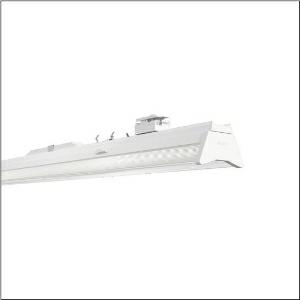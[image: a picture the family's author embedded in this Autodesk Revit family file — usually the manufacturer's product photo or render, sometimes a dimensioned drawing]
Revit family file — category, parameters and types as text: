
# Revit family: licross_r__21_performance_ho_52td16cn4c5m_c92a
name_source: partatom
category: Lighting Fixtures
units: mm (PartAtom-declared; Revit-internal decimal feet)

## family parameters
Cut with Voids When Loaded = No
Host = Face
Light Source = No
Part Type = Normal
Room Calculation Point = No
Round Connector Dimension = Use Diameter
Shared = No

## types (1)
- --- (1 x LED, 12610 lm, 68.9 W, 4000K)
    Apparent Load = 69 VA
    CIE Flux Codes = 63 87 95 78 100
    Color Rendering = 80
    Color Temperature = 4000K
    Default Elevation = 1800 mm
    Description = Licross® 21 Performance HO, luminaire insert, of sheet steel, galvanised, coil coated, white, length: 1.500mm, width: 120mm, height: 123mm, LED rated luminous flux: 12.610lm, light colour: 840, control gear: ON/OFF Multilumen, CLOi, control gear: ECG Multilumen, with plug, 3-pole, with phase selection, mains connection: 220..240V, AC, 50/60Hz, start of lifetime: 69W, end of service life: 83W, internal wiring halogen-free, primary light control with lens, of plastic, primary optical cover: cover, of PMMA, light emission: direct/indirect distribution, primary light characteristic: symmetric, protection rating (complete): IP54, insulation class (complete): insulation class I (protective earthing), certification: CE, ENEC, UKCA, protection symbol: D if used in an environment with non-conductive dust loads with corresponding accessories, impact resistance: IK06, permissible ambient temperature for indoor applications: -35..+35°C, corresponds to IFS (International Featured Standards) requirements for safety and quality in the food industry, reducing of maximum allowable ambient temperature of 5°C with ceiling mounting, LABS conformity tested according to VDMA 24364:2018-05, packaging unit: 1 piece
    Height = 114 mm
    Lamp = 1 x LED
    Lamp Light Flux = 12610 lm
    Lamp Power = 68.9 W
    Lamp count = 1
    Length = 1500 mm
    Luminous efficacy = 183 lm/W
    Manufacturer = Siteco
    ModVariant = No
    Model = 52TD16CN4C5M
    Mounting Place = Ceiling
    Mounting Type = Pendant
    Number of Poles = 1
    OnlyDefault = Yes
    Power Factor = 1
    Product Name = Licross® 21 Performance HO
    Product group = luminaire insert | ceiling pendant
    ProductGroupID = 902
    Protection Class = Protection class I
    Protection Degree = IP 54
    RLX_Detail_Level = 1
    RLX_Emergency_Light_Flux = 0 lm
    RLX_Emergency_Type = 0
    RLX_Emergency_Type_DB = No
    RlxData = <blob elided: 31861 chars, md5=0ba4e3b1>
    Socket = socket
    Standby Power = 0 W
    System Light Flux = 12610 lm
    System Power = 69 W
    Type Comments = factory setting: luminous flux: 100 % | (A | C | E) | 162 mA
    Type Image = l_1256138.jpg
    URL = http://relux.com
    VarID = @adj_133091
    Voltage = 0 V
    Weight = 0.00 kg
    Width = 120 mm

## geometry (parser evidence)
native form markers: Blend x4, Sweep x13
no freeform markers — native parametric forms only
